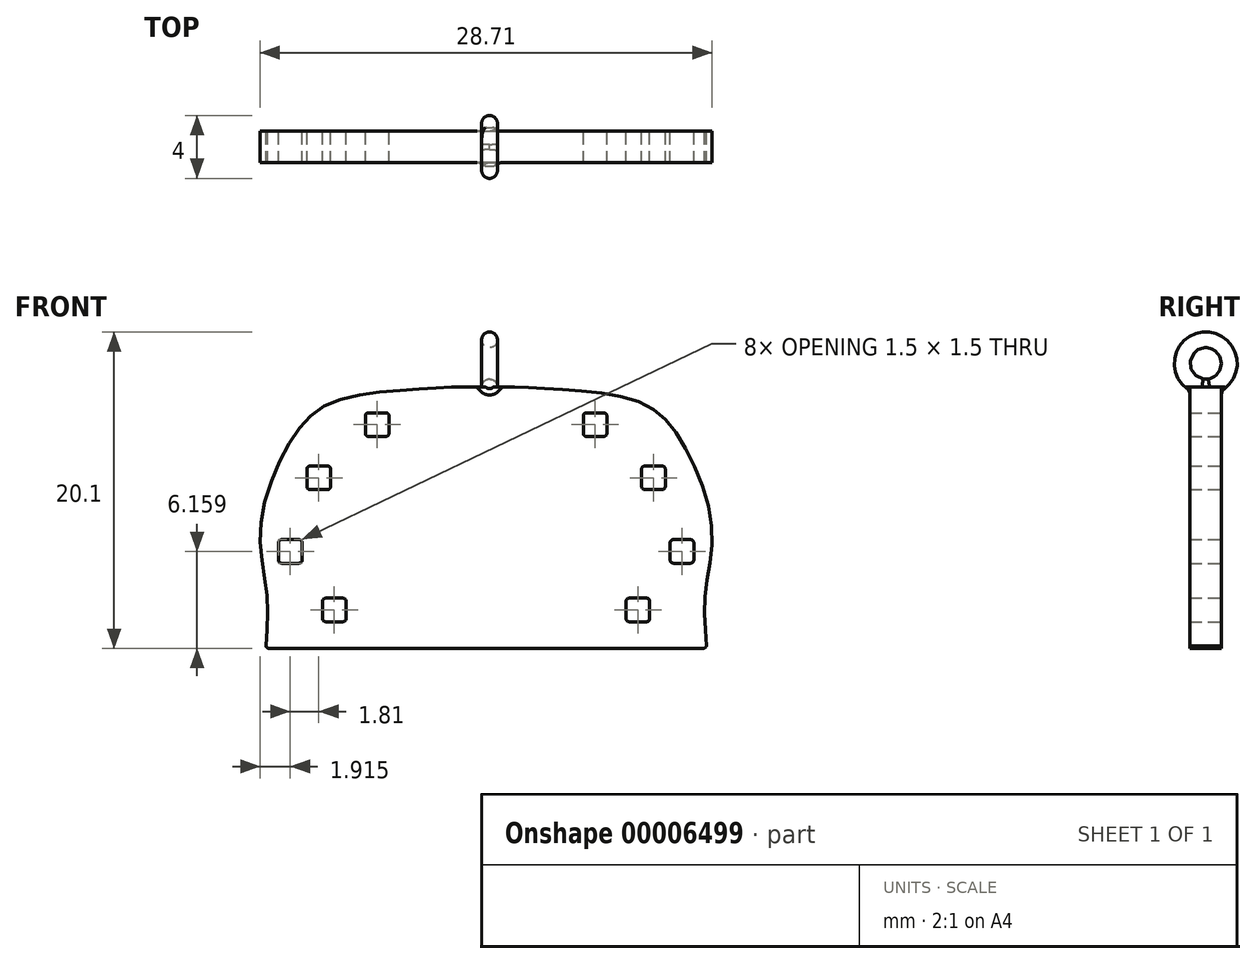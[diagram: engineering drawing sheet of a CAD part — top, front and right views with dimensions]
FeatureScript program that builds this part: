
annotation { "Feature Type Name" : "Feature", "Feature Type Description" : "" }
export const myFeature = defineFeature(function(context is Context, id is Id, definition is map)
    precondition{}
    {
        {
            var Q0;
            Q0=qCreatedBy(makeId("Front.planeOp"),FACE);
            var sketch = newSketch(context, id + "F0", { "sketchPlane" : qUnion([Q0])});
            skFitSpline(sketch, "E0.0", {"points": [v(-0.22, 7.86) * mm, v(-1.98, 7.86) * mm, v(-5.46, 7.65) * mm, v(-10.21, 6.79) * mm, v(-12.74, 4.21) * mm, v(-14.55, -0.98) * mm, v(-14.16, -5.19) * mm, v(-14.22, -8.75) * mm]});
            skFitSpline(sketch, "E0.1", {"points": [v(13.78, -8.75) * mm, v(13.72, -5.19) * mm, v(14.11, -0.98) * mm, v(12.31, 4.21) * mm, v(9.78, 6.79) * mm, v(5.03, 7.65) * mm, v(1.55, 7.86) * mm, v(-0.22, 7.86) * mm]});
            skFitSpline(sketch, "E0.2", {"points": [v(-1.13, 7.85) * mm, v(-0.88, 7.85) * mm, v(-0.64, 7.86) * mm, v(-0.39, 7.86) * mm]});
            skFitSpline(sketch, "E0.3", {"points": [v(-0.04, 7.86) * mm, v(0.2, 7.86) * mm, v(0.45, 7.85) * mm, v(0.7, 7.85) * mm]});
            skArc(sketch, "E0.4", {"start": v(-14.21, -8.54) * mm, "mid": v(-14.16, -8.69) * mm, "end": v(-14.01, -8.75) * mm});
            skArc(sketch, "E1.0", {"start": v(13.58, -8.75) * mm, "mid": v(13.72, -8.69) * mm, "end": v(13.78, -8.54) * mm});
            skLineSegment(sketch, "E2.0", {"start": v(-14.01, -8.75) * mm, "end": v(13.58, -8.75) * mm});
            skFitSpline(sketch, "E3.0", {"points": [v(-0.22, 5.42) * mm, v(-1.29, 5.42) * mm, v(-3.2, 5.36) * mm, v(-6.1, 4.36) * mm, v(-8.13, 1.08) * mm, v(-8.75, -3.32) * mm, v(-8.21, -6.4) * mm, v(-7.84, -7.75) * mm]});
            skFitSpline(sketch, "E3.1", {"points": [v(7.4, -7.75) * mm, v(7.78, -6.4) * mm, v(8.32, -3.32) * mm, v(7.7, 1.08) * mm, v(5.66, 4.36) * mm, v(2.76, 5.36) * mm, v(0.86, 5.42) * mm, v(-0.22, 5.42) * mm]});
            skLineSegment(sketch, "E3.2", {"start": v(-7.69, -7.75) * mm, "end": v(7.25, -7.75) * mm});
            skArc(sketch, "E3.3", {"start": v(7.45, -7.6) * mm, "mid": v(7.38, -7.7) * mm, "end": v(7.25, -7.75) * mm});
            skArc(sketch, "E3.4", {"start": v(-7.69, -7.75) * mm, "mid": v(-7.8, -7.7) * mm, "end": v(-7.88, -7.6) * mm});
            skLineSegment(sketch, "E4.0", {"start": v(-10.4, -7.06) * mm, "end": v(-9.3, -7.06) * mm});
            skArc(sketch, "E4.1", {"start": v(-9.1, -6.86) * mm, "mid": v(-9.16, -7) * mm, "end": v(-9.3, -7.06) * mm});
            skLineSegment(sketch, "E4.2", {"start": v(-9.1, -6.86) * mm, "end": v(-9.1, -5.76) * mm});
            skArc(sketch, "E4.3", {"start": v(-9.3, -5.56) * mm, "mid": v(-9.16, -5.62) * mm, "end": v(-9.1, -5.76) * mm});
            skLineSegment(sketch, "E4.4", {"start": v(-9.3, -5.56) * mm, "end": v(-10.4, -5.56) * mm});
            skLineSegment(sketch, "E4.5", {"start": v(-10.6, -5.76) * mm, "end": v(-10.6, -6.86) * mm});
            skArc(sketch, "E4.6", {"start": v(-10.4, -7.06) * mm, "mid": v(-10.55, -7) * mm, "end": v(-10.6, -6.86) * mm});
            skArc(sketch, "E4.7", {"start": v(-10.6, -5.76) * mm, "mid": v(-10.55, -5.62) * mm, "end": v(-10.4, -5.56) * mm});
            skLineSegment(sketch, "E5.0", {"start": v(-12.1, -1.84) * mm, "end": v(-13.2, -1.84) * mm});
            skArc(sketch, "E5.1", {"start": v(-12.1, -1.84) * mm, "mid": v(-11.96, -1.9) * mm, "end": v(-11.9, -2.04) * mm});
            skLineSegment(sketch, "E5.2", {"start": v(-11.9, -3.14) * mm, "end": v(-11.9, -2.04) * mm});
            skArc(sketch, "E5.3", {"start": v(-11.9, -3.14) * mm, "mid": v(-11.96, -3.28) * mm, "end": v(-12.1, -3.34) * mm});
            skLineSegment(sketch, "E5.4", {"start": v(-13.2, -3.34) * mm, "end": v(-12.1, -3.34) * mm});
            skArc(sketch, "E5.5", {"start": v(-13.4, -2.04) * mm, "mid": v(-13.35, -1.9) * mm, "end": v(-13.2, -1.84) * mm});
            skLineSegment(sketch, "E5.6", {"start": v(-13.4, -2.04) * mm, "end": v(-13.4, -3.14) * mm});
            skArc(sketch, "E5.7", {"start": v(-13.2, -3.34) * mm, "mid": v(-13.35, -3.28) * mm, "end": v(-13.4, -3.14) * mm});
            skLineSegment(sketch, "E6.0", {"start": v(-10.3, 2.83) * mm, "end": v(-11.4, 2.83) * mm});
            skArc(sketch, "E6.1", {"start": v(-11.6, 2.63) * mm, "mid": v(-11.54, 2.77) * mm, "end": v(-11.4, 2.83) * mm});
            skLineSegment(sketch, "E6.2", {"start": v(-11.6, 2.63) * mm, "end": v(-11.6, 1.53) * mm});
            skArc(sketch, "E6.3", {"start": v(-11.4, 1.33) * mm, "mid": v(-11.54, 1.4) * mm, "end": v(-11.6, 1.53) * mm});
            skLineSegment(sketch, "E6.4", {"start": v(-11.4, 1.33) * mm, "end": v(-10.3, 1.33) * mm});
            skArc(sketch, "E6.5", {"start": v(-10.1, 1.53) * mm, "mid": v(-10.15, 1.4) * mm, "end": v(-10.3, 1.33) * mm});
            skLineSegment(sketch, "E6.6", {"start": v(-10.1, 1.53) * mm, "end": v(-10.1, 2.63) * mm});
            skArc(sketch, "E6.7", {"start": v(-10.3, 2.83) * mm, "mid": v(-10.15, 2.77) * mm, "end": v(-10.1, 2.63) * mm});
            skLineSegment(sketch, "E7.0", {"start": v(-6.59, 6.21) * mm, "end": v(-7.69, 6.21) * mm});
            skLineSegment(sketch, "E7.1", {"start": v(-7.69, 4.71) * mm, "end": v(-6.59, 4.71) * mm});
            skArc(sketch, "E7.2", {"start": v(-6.39, 4.91) * mm, "mid": v(-6.44, 4.77) * mm, "end": v(-6.59, 4.71) * mm});
            skLineSegment(sketch, "E7.3", {"start": v(-6.39, 4.91) * mm, "end": v(-6.39, 6.01) * mm});
            skArc(sketch, "E7.4", {"start": v(-6.59, 6.21) * mm, "mid": v(-6.44, 6.15) * mm, "end": v(-6.39, 6.01) * mm});
            skArc(sketch, "E7.5", {"start": v(-7.89, 6.01) * mm, "mid": v(-7.83, 6.15) * mm, "end": v(-7.69, 6.21) * mm});
            skLineSegment(sketch, "E7.6", {"start": v(-7.89, 6.01) * mm, "end": v(-7.89, 4.91) * mm});
            skArc(sketch, "E7.7", {"start": v(-7.69, 4.71) * mm, "mid": v(-7.83, 4.77) * mm, "end": v(-7.89, 4.91) * mm});
            skLineSegment(sketch, "E8.0", {"start": v(7.25, 6.21) * mm, "end": v(6.15, 6.21) * mm});
            skArc(sketch, "E8.1", {"start": v(5.95, 6.01) * mm, "mid": v(6.01, 6.15) * mm, "end": v(6.15, 6.21) * mm});
            skLineSegment(sketch, "E8.2", {"start": v(5.95, 6.01) * mm, "end": v(5.95, 4.91) * mm});
            skArc(sketch, "E8.3", {"start": v(6.15, 4.71) * mm, "mid": v(6.01, 4.77) * mm, "end": v(5.95, 4.91) * mm});
            skLineSegment(sketch, "E8.4", {"start": v(6.15, 4.71) * mm, "end": v(7.25, 4.71) * mm});
            skArc(sketch, "E8.5", {"start": v(7.45, 4.91) * mm, "mid": v(7.4, 4.77) * mm, "end": v(7.25, 4.71) * mm});
            skLineSegment(sketch, "E8.6", {"start": v(7.45, 4.91) * mm, "end": v(7.45, 6.01) * mm});
            skArc(sketch, "E8.7", {"start": v(7.25, 6.21) * mm, "mid": v(7.4, 6.15) * mm, "end": v(7.45, 6.01) * mm});
            skLineSegment(sketch, "E9.0", {"start": v(10.96, 2.83) * mm, "end": v(9.86, 2.83) * mm});
            skArc(sketch, "E9.1", {"start": v(9.66, 2.63) * mm, "mid": v(9.72, 2.77) * mm, "end": v(9.86, 2.83) * mm});
            skLineSegment(sketch, "E9.2", {"start": v(9.66, 2.63) * mm, "end": v(9.66, 1.53) * mm});
            skArc(sketch, "E9.3", {"start": v(9.86, 1.33) * mm, "mid": v(9.72, 1.4) * mm, "end": v(9.66, 1.53) * mm});
            skLineSegment(sketch, "E9.4", {"start": v(9.86, 1.33) * mm, "end": v(10.96, 1.33) * mm});
            skArc(sketch, "E9.5", {"start": v(11.16, 1.53) * mm, "mid": v(11.1, 1.4) * mm, "end": v(10.96, 1.33) * mm});
            skLineSegment(sketch, "E9.6", {"start": v(11.16, 1.53) * mm, "end": v(11.16, 2.63) * mm});
            skArc(sketch, "E9.7", {"start": v(10.96, 2.83) * mm, "mid": v(11.1, 2.77) * mm, "end": v(11.16, 2.63) * mm});
            skLineSegment(sketch, "E10.0", {"start": v(12.77, -1.84) * mm, "end": v(11.67, -1.84) * mm});
            skArc(sketch, "E10.1", {"start": v(11.47, -2.04) * mm, "mid": v(11.53, -1.9) * mm, "end": v(11.67, -1.84) * mm});
            skLineSegment(sketch, "E10.2", {"start": v(11.47, -2.04) * mm, "end": v(11.47, -3.14) * mm});
            skArc(sketch, "E10.3", {"start": v(11.67, -3.34) * mm, "mid": v(11.53, -3.28) * mm, "end": v(11.47, -3.14) * mm});
            skLineSegment(sketch, "E10.4", {"start": v(11.67, -3.34) * mm, "end": v(12.77, -3.34) * mm});
            skArc(sketch, "E10.5", {"start": v(12.97, -3.14) * mm, "mid": v(12.91, -3.28) * mm, "end": v(12.77, -3.34) * mm});
            skLineSegment(sketch, "E10.6", {"start": v(12.97, -3.14) * mm, "end": v(12.97, -2.04) * mm});
            skArc(sketch, "E10.7", {"start": v(12.77, -1.84) * mm, "mid": v(12.91, -1.9) * mm, "end": v(12.97, -2.04) * mm});
            skLineSegment(sketch, "E11.0", {"start": v(9.97, -5.56) * mm, "end": v(8.87, -5.56) * mm});
            skArc(sketch, "E11.1", {"start": v(8.67, -5.76) * mm, "mid": v(8.73, -5.62) * mm, "end": v(8.87, -5.56) * mm});
            skLineSegment(sketch, "E11.2", {"start": v(8.67, -5.76) * mm, "end": v(8.67, -6.86) * mm});
            skArc(sketch, "E11.3", {"start": v(8.87, -7.06) * mm, "mid": v(8.73, -7) * mm, "end": v(8.67, -6.86) * mm});
            skLineSegment(sketch, "E11.4", {"start": v(8.87, -7.06) * mm, "end": v(9.97, -7.06) * mm});
            skArc(sketch, "E11.5", {"start": v(10.17, -6.86) * mm, "mid": v(10.12, -7) * mm, "end": v(9.97, -7.06) * mm});
            skLineSegment(sketch, "E11.6", {"start": v(10.17, -6.86) * mm, "end": v(10.17, -5.76) * mm});
            skArc(sketch, "E11.7", {"start": v(9.97, -5.56) * mm, "mid": v(10.12, -5.62) * mm, "end": v(10.17, -5.76) * mm});
            skArc(sketch, "E12", {"start": v(-0.04, 7.86) * mm, "mid": v(-0.22, 7.86) * mm, "end": v(-0.39, 7.86) * mm});
            skSolve(sketch);
        }
        {
            var Q0;
            Q0=makeQuery(id+"F0.imprint","IMPRINT",FACE,{"disambiguationData":[TD([[makeQuery(id+"F0.imprint","IMPRINT",EDGE,{"derivedFrom":sQuery(id+"F0.wireOp",EDGE,"E0.0")}),1.0]])]});
            var Q1;
            Q1=sQuery(id+"F0.wireOp",EDGE,"E0.0");
            var Q2;
            Q2=sQuery(id+"F0.wireOp",EDGE,"E0.1");
            var Q3;
            Q3=sQuery(id+"F0.wireOp",EDGE,"E0.2");
            var Q4;
            Q4=sQuery(id+"F0.wireOp",EDGE,"E0.3");
            var Q5;
            Q5=sQuery(id+"F0.wireOp",EDGE,"E0.4");
            var Q6;
            Q6=sQuery(id+"F0.wireOp",EDGE,"E1.0");
            var Q7;
            Q7=sQuery(id+"F0.wireOp",EDGE,"E2.0");
            var Q8;
            Q8=sQuery(id+"F0.wireOp",EDGE,"E3.0");
            var Q9;
            Q9=sQuery(id+"F0.wireOp",EDGE,"E3.1");
            var Q10;
            Q10=sQuery(id+"F0.wireOp",EDGE,"E3.2");
            var Q11;
            Q11=sQuery(id+"F0.wireOp",EDGE,"E3.3");
            var Q12;
            Q12=sQuery(id+"F0.wireOp",EDGE,"E3.4");
            var Q13;
            Q13=sQuery(id+"F0.wireOp",EDGE,"E4.0");
            var Q14;
            Q14=sQuery(id+"F0.wireOp",EDGE,"E4.1");
            var Q15;
            Q15=sQuery(id+"F0.wireOp",EDGE,"E4.2");
            var Q16;
            Q16=sQuery(id+"F0.wireOp",EDGE,"E4.3");
            var Q17;
            Q17=sQuery(id+"F0.wireOp",EDGE,"E4.4");
            var Q18;
            Q18=sQuery(id+"F0.wireOp",EDGE,"E4.5");
            var Q19;
            Q19=sQuery(id+"F0.wireOp",EDGE,"E4.6");
            var Q20;
            Q20=sQuery(id+"F0.wireOp",EDGE,"E4.7");
            var Q21;
            Q21=sQuery(id+"F0.wireOp",EDGE,"E5.0");
            var Q22;
            Q22=sQuery(id+"F0.wireOp",EDGE,"E5.1");
            var Q23;
            Q23=sQuery(id+"F0.wireOp",EDGE,"E5.2");
            var Q24;
            Q24=sQuery(id+"F0.wireOp",EDGE,"E5.3");
            var Q25;
            Q25=sQuery(id+"F0.wireOp",EDGE,"E5.4");
            var Q26;
            Q26=sQuery(id+"F0.wireOp",EDGE,"E5.5");
            var Q27;
            Q27=sQuery(id+"F0.wireOp",EDGE,"E5.6");
            var Q28;
            Q28=sQuery(id+"F0.wireOp",EDGE,"E5.7");
            var Q29;
            Q29=sQuery(id+"F0.wireOp",EDGE,"E6.0");
            var Q30;
            Q30=sQuery(id+"F0.wireOp",EDGE,"E6.1");
            var Q31;
            Q31=sQuery(id+"F0.wireOp",EDGE,"E6.2");
            var Q32;
            Q32=sQuery(id+"F0.wireOp",EDGE,"E6.3");
            var Q33;
            Q33=sQuery(id+"F0.wireOp",EDGE,"E6.4");
            var Q34;
            Q34=sQuery(id+"F0.wireOp",EDGE,"E6.5");
            var Q35;
            Q35=sQuery(id+"F0.wireOp",EDGE,"E6.6");
            var Q36;
            Q36=sQuery(id+"F0.wireOp",EDGE,"E6.7");
            var Q37;
            Q37=sQuery(id+"F0.wireOp",EDGE,"E7.0");
            var Q38;
            Q38=sQuery(id+"F0.wireOp",EDGE,"E7.1");
            var Q39;
            Q39=sQuery(id+"F0.wireOp",EDGE,"E7.2");
            var Q40;
            Q40=sQuery(id+"F0.wireOp",EDGE,"E7.3");
            var Q41;
            Q41=sQuery(id+"F0.wireOp",EDGE,"E7.4");
            var Q42;
            Q42=sQuery(id+"F0.wireOp",EDGE,"E7.5");
            var Q43;
            Q43=sQuery(id+"F0.wireOp",EDGE,"E7.6");
            var Q44;
            Q44=sQuery(id+"F0.wireOp",EDGE,"E7.7");
            var Q45;
            Q45=sQuery(id+"F0.wireOp",EDGE,"E8.0");
            var Q46;
            Q46=sQuery(id+"F0.wireOp",EDGE,"E8.1");
            var Q47;
            Q47=sQuery(id+"F0.wireOp",EDGE,"E8.2");
            var Q48;
            Q48=sQuery(id+"F0.wireOp",EDGE,"E8.3");
            var Q49;
            Q49=sQuery(id+"F0.wireOp",EDGE,"E8.4");
            var Q50;
            Q50=sQuery(id+"F0.wireOp",EDGE,"E8.5");
            var Q51;
            Q51=sQuery(id+"F0.wireOp",EDGE,"E8.6");
            var Q52;
            Q52=sQuery(id+"F0.wireOp",EDGE,"E8.7");
            var Q53;
            Q53=sQuery(id+"F0.wireOp",EDGE,"E9.0");
            var Q54;
            Q54=sQuery(id+"F0.wireOp",EDGE,"E9.1");
            var Q55;
            Q55=sQuery(id+"F0.wireOp",EDGE,"E9.2");
            var Q56;
            Q56=sQuery(id+"F0.wireOp",EDGE,"E9.3");
            var Q57;
            Q57=sQuery(id+"F0.wireOp",EDGE,"E9.4");
            var Q58;
            Q58=sQuery(id+"F0.wireOp",EDGE,"E9.5");
            var Q59;
            Q59=sQuery(id+"F0.wireOp",EDGE,"E9.6");
            var Q60;
            Q60=sQuery(id+"F0.wireOp",EDGE,"E9.7");
            var Q61;
            Q61=sQuery(id+"F0.wireOp",EDGE,"E10.0");
            var Q62;
            Q62=sQuery(id+"F0.wireOp",EDGE,"E10.1");
            var Q63;
            Q63=sQuery(id+"F0.wireOp",EDGE,"E10.2");
            var Q64;
            Q64=sQuery(id+"F0.wireOp",EDGE,"E10.3");
            var Q65;
            Q65=sQuery(id+"F0.wireOp",EDGE,"E10.4");
            var Q66;
            Q66=sQuery(id+"F0.wireOp",EDGE,"E10.5");
            var Q67;
            Q67=sQuery(id+"F0.wireOp",EDGE,"E10.6");
            var Q68;
            Q68=sQuery(id+"F0.wireOp",EDGE,"E10.7");
            var Q69;
            Q69=sQuery(id+"F0.wireOp",EDGE,"E11.0");
            var Q70;
            Q70=sQuery(id+"F0.wireOp",EDGE,"E11.1");
            var Q71;
            Q71=sQuery(id+"F0.wireOp",EDGE,"E11.2");
            var Q72;
            Q72=sQuery(id+"F0.wireOp",EDGE,"E11.3");
            var Q73;
            Q73=sQuery(id+"F0.wireOp",EDGE,"E11.4");
            var Q74;
            Q74=sQuery(id+"F0.wireOp",EDGE,"E11.5");
            var Q75;
            Q75=sQuery(id+"F0.wireOp",EDGE,"E11.6");
            var Q76;
            Q76=sQuery(id+"F0.wireOp",EDGE,"E11.7");
            var Q77;
            Q77=sQuery(id+"F0.wireOp",EDGE,"E12");
            extrude(context, id + "F1", {"entities" : qUnion([Q0]), "surfaceEntities" : qUnion([Q1, Q2, Q3, Q4, Q5, Q6, Q7, Q8, Q9, Q10, Q11, Q12, Q13, Q14, Q15, Q16, Q17, Q18, Q19, Q20, Q21, Q22, Q23, Q24, Q25, Q26, Q27, Q28, Q29, Q30, Q31, Q32, Q33, Q34, Q35, Q36, Q37, Q38, Q39, Q40, Q41, Q42, Q43, Q44, Q45, Q46, Q47, Q48, Q49, Q50, Q51, Q52, Q53, Q54, Q55, Q56, Q57, Q58, Q59, Q60, Q61, Q62, Q63, Q64, Q65, Q66, Q67, Q68, Q69, Q70, Q71, Q72, Q73, Q74, Q75, Q76, Q77]), "endBound" : BoundingType.SYMMETRIC, "depth" : 2 * mm});
        }
        {
            var Q0;
            Q0=qCreatedBy(makeId("Right.planeOp"),FACE);
            var sketch = newSketch(context, id + "F2", { "sketchPlane" : qUnion([Q0])});
            skCircle(sketch, "E13", {"center": v(0, 9.35) * mm, "radius": 2 * mm});
            skCircle(sketch, "E14", {"center": v(0, 9.35) * mm, "radius": 1 * mm});
            skSolve(sketch);
        }
        {
            var Q0;
            Q0 = qSketchRegion(id + "F2", true);
            extrude(context, id + "F3", {"entities" : qUnion([Q0]), "operationType" : NewBodyOperationType.ADD, "endBound" : BoundingType.SYMMETRIC, "depth" : 1 * mm});
        }
        {
            var Q0;
            Q0=makeQuery(id+"F3.opExtrude","CAP_EDGE",EDGE,{"disambiguationData":[OSD([sQuery(id+"F2.wireOp",EDGE,"E13")])],"isStart":false});
            var Q1;
            Q1=makeQuery(id+"F3.opExtrude","CAP_EDGE",EDGE,{"disambiguationData":[OSD([sQuery(id+"F2.wireOp",EDGE,"E13")])],"isStart":true});
            fillet(context, id + "F4", {"entities" : qUnion([Q0, Q1]), "radius" : 0.5 * mm, "tangentPropagation" : true, "allowEdgeOverflow" : false});
        }
        {
            var Q0;
            Q0=makeQuery(id+"F4.opFillet","BLEND_EDGE",EDGE,{"blendedFrom":[makeQuery(id+"F3.opExtrude","CAP_EDGE",EDGE,{"disambiguationData":[OSD([sQuery(id+"F2.wireOp",EDGE,"E13")])],"isStart":false}),makeQuery(id+"F1.opExtrude","CAP_FACE",FACE,{"disambiguationData":[OSD([sQuery(id+"F0.wireOp",EDGE,"E0.0"),sQuery(id+"F0.wireOp",EDGE,"E0.1"),sQuery(id+"F0.wireOp",EDGE,"E0.2"),sQuery(id+"F0.wireOp",EDGE,"E0.3"),sQuery(id+"F0.wireOp",EDGE,"E0.4"),sQuery(id+"F0.wireOp",EDGE,"E1.0"),sQuery(id+"F0.wireOp",EDGE,"E2.0"),sQuery(id+"F0.wireOp",EDGE,"E3.0"),sQuery(id+"F0.wireOp",EDGE,"E3.1"),sQuery(id+"F0.wireOp",EDGE,"E3.2"),sQuery(id+"F0.wireOp",EDGE,"E3.3"),sQuery(id+"F0.wireOp",EDGE,"E3.4"),sQuery(id+"F0.wireOp",EDGE,"E4.0"),sQuery(id+"F0.wireOp",EDGE,"E4.1"),sQuery(id+"F0.wireOp",EDGE,"E4.2"),sQuery(id+"F0.wireOp",EDGE,"E4.3"),sQuery(id+"F0.wireOp",EDGE,"E4.4"),sQuery(id+"F0.wireOp",EDGE,"E4.5"),sQuery(id+"F0.wireOp",EDGE,"E4.6"),sQuery(id+"F0.wireOp",EDGE,"E4.7"),sQuery(id+"F0.wireOp",EDGE,"E5.0"),sQuery(id+"F0.wireOp",EDGE,"E5.1"),sQuery(id+"F0.wireOp",EDGE,"E5.2"),sQuery(id+"F0.wireOp",EDGE,"E5.3"),sQuery(id+"F0.wireOp",EDGE,"E5.4"),sQuery(id+"F0.wireOp",EDGE,"E5.5"),sQuery(id+"F0.wireOp",EDGE,"E5.6"),sQuery(id+"F0.wireOp",EDGE,"E5.7"),sQuery(id+"F0.wireOp",EDGE,"E6.0"),sQuery(id+"F0.wireOp",EDGE,"E6.1"),sQuery(id+"F0.wireOp",EDGE,"E6.2"),sQuery(id+"F0.wireOp",EDGE,"E6.3"),sQuery(id+"F0.wireOp",EDGE,"E6.4"),sQuery(id+"F0.wireOp",EDGE,"E6.5"),sQuery(id+"F0.wireOp",EDGE,"E6.6"),sQuery(id+"F0.wireOp",EDGE,"E6.7"),sQuery(id+"F0.wireOp",EDGE,"E7.0"),sQuery(id+"F0.wireOp",EDGE,"E7.1"),sQuery(id+"F0.wireOp",EDGE,"E7.2"),sQuery(id+"F0.wireOp",EDGE,"E7.3"),sQuery(id+"F0.wireOp",EDGE,"E7.4"),sQuery(id+"F0.wireOp",EDGE,"E7.5"),sQuery(id+"F0.wireOp",EDGE,"E7.6"),sQuery(id+"F0.wireOp",EDGE,"E7.7"),sQuery(id+"F0.wireOp",EDGE,"E8.0"),sQuery(id+"F0.wireOp",EDGE,"E8.1"),sQuery(id+"F0.wireOp",EDGE,"E8.2"),sQuery(id+"F0.wireOp",EDGE,"E8.3"),sQuery(id+"F0.wireOp",EDGE,"E8.4"),sQuery(id+"F0.wireOp",EDGE,"E8.5"),sQuery(id+"F0.wireOp",EDGE,"E8.6"),sQuery(id+"F0.wireOp",EDGE,"E8.7"),sQuery(id+"F0.wireOp",EDGE,"E9.0"),sQuery(id+"F0.wireOp",EDGE,"E9.1"),sQuery(id+"F0.wireOp",EDGE,"E9.2"),sQuery(id+"F0.wireOp",EDGE,"E9.3"),sQuery(id+"F0.wireOp",EDGE,"E9.4"),sQuery(id+"F0.wireOp",EDGE,"E9.5"),sQuery(id+"F0.wireOp",EDGE,"E9.6"),sQuery(id+"F0.wireOp",EDGE,"E9.7"),sQuery(id+"F0.wireOp",EDGE,"E10.0"),sQuery(id+"F0.wireOp",EDGE,"E10.1"),sQuery(id+"F0.wireOp",EDGE,"E10.2"),sQuery(id+"F0.wireOp",EDGE,"E10.3"),sQuery(id+"F0.wireOp",EDGE,"E10.4"),sQuery(id+"F0.wireOp",EDGE,"E10.5"),sQuery(id+"F0.wireOp",EDGE,"E10.6"),sQuery(id+"F0.wireOp",EDGE,"E10.7"),sQuery(id+"F0.wireOp",EDGE,"E11.0"),sQuery(id+"F0.wireOp",EDGE,"E11.1"),sQuery(id+"F0.wireOp",EDGE,"E11.2"),sQuery(id+"F0.wireOp",EDGE,"E11.3"),sQuery(id+"F0.wireOp",EDGE,"E11.4"),sQuery(id+"F0.wireOp",EDGE,"E11.5"),sQuery(id+"F0.wireOp",EDGE,"E11.6"),sQuery(id+"F0.wireOp",EDGE,"E11.7"),sQuery(id+"F0.wireOp",EDGE,"E12")])],"isStart":false})],"blendedInto":[makeQuery(id+"F1.opExtrude","CAP_FACE",FACE,{"disambiguationData":[OSD([sQuery(id+"F0.wireOp",EDGE,"E0.0"),sQuery(id+"F0.wireOp",EDGE,"E0.1"),sQuery(id+"F0.wireOp",EDGE,"E0.2"),sQuery(id+"F0.wireOp",EDGE,"E0.3"),sQuery(id+"F0.wireOp",EDGE,"E0.4"),sQuery(id+"F0.wireOp",EDGE,"E1.0"),sQuery(id+"F0.wireOp",EDGE,"E2.0"),sQuery(id+"F0.wireOp",EDGE,"E3.0"),sQuery(id+"F0.wireOp",EDGE,"E3.1"),sQuery(id+"F0.wireOp",EDGE,"E3.2"),sQuery(id+"F0.wireOp",EDGE,"E3.3"),sQuery(id+"F0.wireOp",EDGE,"E3.4"),sQuery(id+"F0.wireOp",EDGE,"E4.0"),sQuery(id+"F0.wireOp",EDGE,"E4.1"),sQuery(id+"F0.wireOp",EDGE,"E4.2"),sQuery(id+"F0.wireOp",EDGE,"E4.3"),sQuery(id+"F0.wireOp",EDGE,"E4.4"),sQuery(id+"F0.wireOp",EDGE,"E4.5"),sQuery(id+"F0.wireOp",EDGE,"E4.6"),sQuery(id+"F0.wireOp",EDGE,"E4.7"),sQuery(id+"F0.wireOp",EDGE,"E5.0"),sQuery(id+"F0.wireOp",EDGE,"E5.1"),sQuery(id+"F0.wireOp",EDGE,"E5.2"),sQuery(id+"F0.wireOp",EDGE,"E5.3"),sQuery(id+"F0.wireOp",EDGE,"E5.4"),sQuery(id+"F0.wireOp",EDGE,"E5.5"),sQuery(id+"F0.wireOp",EDGE,"E5.6"),sQuery(id+"F0.wireOp",EDGE,"E5.7"),sQuery(id+"F0.wireOp",EDGE,"E6.0"),sQuery(id+"F0.wireOp",EDGE,"E6.1"),sQuery(id+"F0.wireOp",EDGE,"E6.2"),sQuery(id+"F0.wireOp",EDGE,"E6.3"),sQuery(id+"F0.wireOp",EDGE,"E6.4"),sQuery(id+"F0.wireOp",EDGE,"E6.5"),sQuery(id+"F0.wireOp",EDGE,"E6.6"),sQuery(id+"F0.wireOp",EDGE,"E6.7"),sQuery(id+"F0.wireOp",EDGE,"E7.0"),sQuery(id+"F0.wireOp",EDGE,"E7.1"),sQuery(id+"F0.wireOp",EDGE,"E7.2"),sQuery(id+"F0.wireOp",EDGE,"E7.3"),sQuery(id+"F0.wireOp",EDGE,"E7.4"),sQuery(id+"F0.wireOp",EDGE,"E7.5"),sQuery(id+"F0.wireOp",EDGE,"E7.6"),sQuery(id+"F0.wireOp",EDGE,"E7.7"),sQuery(id+"F0.wireOp",EDGE,"E8.0"),sQuery(id+"F0.wireOp",EDGE,"E8.1"),sQuery(id+"F0.wireOp",EDGE,"E8.2"),sQuery(id+"F0.wireOp",EDGE,"E8.3"),sQuery(id+"F0.wireOp",EDGE,"E8.4"),sQuery(id+"F0.wireOp",EDGE,"E8.5"),sQuery(id+"F0.wireOp",EDGE,"E8.6"),sQuery(id+"F0.wireOp",EDGE,"E8.7"),sQuery(id+"F0.wireOp",EDGE,"E9.0"),sQuery(id+"F0.wireOp",EDGE,"E9.1"),sQuery(id+"F0.wireOp",EDGE,"E9.2"),sQuery(id+"F0.wireOp",EDGE,"E9.3"),sQuery(id+"F0.wireOp",EDGE,"E9.4"),sQuery(id+"F0.wireOp",EDGE,"E9.5"),sQuery(id+"F0.wireOp",EDGE,"E9.6"),sQuery(id+"F0.wireOp",EDGE,"E9.7"),sQuery(id+"F0.wireOp",EDGE,"E10.0"),sQuery(id+"F0.wireOp",EDGE,"E10.1"),sQuery(id+"F0.wireOp",EDGE,"E10.2"),sQuery(id+"F0.wireOp",EDGE,"E10.3"),sQuery(id+"F0.wireOp",EDGE,"E10.4"),sQuery(id+"F0.wireOp",EDGE,"E10.5"),sQuery(id+"F0.wireOp",EDGE,"E10.6"),sQuery(id+"F0.wireOp",EDGE,"E10.7"),sQuery(id+"F0.wireOp",EDGE,"E11.0"),sQuery(id+"F0.wireOp",EDGE,"E11.1"),sQuery(id+"F0.wireOp",EDGE,"E11.2"),sQuery(id+"F0.wireOp",EDGE,"E11.3"),sQuery(id+"F0.wireOp",EDGE,"E11.4"),sQuery(id+"F0.wireOp",EDGE,"E11.5"),sQuery(id+"F0.wireOp",EDGE,"E11.6"),sQuery(id+"F0.wireOp",EDGE,"E11.7"),sQuery(id+"F0.wireOp",EDGE,"E12")])],"isStart":false})]});
            var Q1;
            Q1=makeQuery(id+"F4.opFillet","BLEND_EDGE",EDGE,{"blendedFrom":[makeQuery(id+"F3.opExtrude","CAP_EDGE",EDGE,{"disambiguationData":[OSD([sQuery(id+"F2.wireOp",EDGE,"E13")])],"isStart":true}),makeQuery(id+"F1.opExtrude","CAP_FACE",FACE,{"disambiguationData":[OSD([sQuery(id+"F0.wireOp",EDGE,"E0.0"),sQuery(id+"F0.wireOp",EDGE,"E0.1"),sQuery(id+"F0.wireOp",EDGE,"E0.2"),sQuery(id+"F0.wireOp",EDGE,"E0.3"),sQuery(id+"F0.wireOp",EDGE,"E0.4"),sQuery(id+"F0.wireOp",EDGE,"E1.0"),sQuery(id+"F0.wireOp",EDGE,"E2.0"),sQuery(id+"F0.wireOp",EDGE,"E3.0"),sQuery(id+"F0.wireOp",EDGE,"E3.1"),sQuery(id+"F0.wireOp",EDGE,"E3.2"),sQuery(id+"F0.wireOp",EDGE,"E3.3"),sQuery(id+"F0.wireOp",EDGE,"E3.4"),sQuery(id+"F0.wireOp",EDGE,"E4.0"),sQuery(id+"F0.wireOp",EDGE,"E4.1"),sQuery(id+"F0.wireOp",EDGE,"E4.2"),sQuery(id+"F0.wireOp",EDGE,"E4.3"),sQuery(id+"F0.wireOp",EDGE,"E4.4"),sQuery(id+"F0.wireOp",EDGE,"E4.5"),sQuery(id+"F0.wireOp",EDGE,"E4.6"),sQuery(id+"F0.wireOp",EDGE,"E4.7"),sQuery(id+"F0.wireOp",EDGE,"E5.0"),sQuery(id+"F0.wireOp",EDGE,"E5.1"),sQuery(id+"F0.wireOp",EDGE,"E5.2"),sQuery(id+"F0.wireOp",EDGE,"E5.3"),sQuery(id+"F0.wireOp",EDGE,"E5.4"),sQuery(id+"F0.wireOp",EDGE,"E5.5"),sQuery(id+"F0.wireOp",EDGE,"E5.6"),sQuery(id+"F0.wireOp",EDGE,"E5.7"),sQuery(id+"F0.wireOp",EDGE,"E6.0"),sQuery(id+"F0.wireOp",EDGE,"E6.1"),sQuery(id+"F0.wireOp",EDGE,"E6.2"),sQuery(id+"F0.wireOp",EDGE,"E6.3"),sQuery(id+"F0.wireOp",EDGE,"E6.4"),sQuery(id+"F0.wireOp",EDGE,"E6.5"),sQuery(id+"F0.wireOp",EDGE,"E6.6"),sQuery(id+"F0.wireOp",EDGE,"E6.7"),sQuery(id+"F0.wireOp",EDGE,"E7.0"),sQuery(id+"F0.wireOp",EDGE,"E7.1"),sQuery(id+"F0.wireOp",EDGE,"E7.2"),sQuery(id+"F0.wireOp",EDGE,"E7.3"),sQuery(id+"F0.wireOp",EDGE,"E7.4"),sQuery(id+"F0.wireOp",EDGE,"E7.5"),sQuery(id+"F0.wireOp",EDGE,"E7.6"),sQuery(id+"F0.wireOp",EDGE,"E7.7"),sQuery(id+"F0.wireOp",EDGE,"E8.0"),sQuery(id+"F0.wireOp",EDGE,"E8.1"),sQuery(id+"F0.wireOp",EDGE,"E8.2"),sQuery(id+"F0.wireOp",EDGE,"E8.3"),sQuery(id+"F0.wireOp",EDGE,"E8.4"),sQuery(id+"F0.wireOp",EDGE,"E8.5"),sQuery(id+"F0.wireOp",EDGE,"E8.6"),sQuery(id+"F0.wireOp",EDGE,"E8.7"),sQuery(id+"F0.wireOp",EDGE,"E9.0"),sQuery(id+"F0.wireOp",EDGE,"E9.1"),sQuery(id+"F0.wireOp",EDGE,"E9.2"),sQuery(id+"F0.wireOp",EDGE,"E9.3"),sQuery(id+"F0.wireOp",EDGE,"E9.4"),sQuery(id+"F0.wireOp",EDGE,"E9.5"),sQuery(id+"F0.wireOp",EDGE,"E9.6"),sQuery(id+"F0.wireOp",EDGE,"E9.7"),sQuery(id+"F0.wireOp",EDGE,"E10.0"),sQuery(id+"F0.wireOp",EDGE,"E10.1"),sQuery(id+"F0.wireOp",EDGE,"E10.2"),sQuery(id+"F0.wireOp",EDGE,"E10.3"),sQuery(id+"F0.wireOp",EDGE,"E10.4"),sQuery(id+"F0.wireOp",EDGE,"E10.5"),sQuery(id+"F0.wireOp",EDGE,"E10.6"),sQuery(id+"F0.wireOp",EDGE,"E10.7"),sQuery(id+"F0.wireOp",EDGE,"E11.0"),sQuery(id+"F0.wireOp",EDGE,"E11.1"),sQuery(id+"F0.wireOp",EDGE,"E11.2"),sQuery(id+"F0.wireOp",EDGE,"E11.3"),sQuery(id+"F0.wireOp",EDGE,"E11.4"),sQuery(id+"F0.wireOp",EDGE,"E11.5"),sQuery(id+"F0.wireOp",EDGE,"E11.6"),sQuery(id+"F0.wireOp",EDGE,"E11.7"),sQuery(id+"F0.wireOp",EDGE,"E12")])],"isStart":true})],"blendedInto":[makeQuery(id+"F1.opExtrude","CAP_FACE",FACE,{"disambiguationData":[OSD([sQuery(id+"F0.wireOp",EDGE,"E0.0"),sQuery(id+"F0.wireOp",EDGE,"E0.1"),sQuery(id+"F0.wireOp",EDGE,"E0.2"),sQuery(id+"F0.wireOp",EDGE,"E0.3"),sQuery(id+"F0.wireOp",EDGE,"E0.4"),sQuery(id+"F0.wireOp",EDGE,"E1.0"),sQuery(id+"F0.wireOp",EDGE,"E2.0"),sQuery(id+"F0.wireOp",EDGE,"E3.0"),sQuery(id+"F0.wireOp",EDGE,"E3.1"),sQuery(id+"F0.wireOp",EDGE,"E3.2"),sQuery(id+"F0.wireOp",EDGE,"E3.3"),sQuery(id+"F0.wireOp",EDGE,"E3.4"),sQuery(id+"F0.wireOp",EDGE,"E4.0"),sQuery(id+"F0.wireOp",EDGE,"E4.1"),sQuery(id+"F0.wireOp",EDGE,"E4.2"),sQuery(id+"F0.wireOp",EDGE,"E4.3"),sQuery(id+"F0.wireOp",EDGE,"E4.4"),sQuery(id+"F0.wireOp",EDGE,"E4.5"),sQuery(id+"F0.wireOp",EDGE,"E4.6"),sQuery(id+"F0.wireOp",EDGE,"E4.7"),sQuery(id+"F0.wireOp",EDGE,"E5.0"),sQuery(id+"F0.wireOp",EDGE,"E5.1"),sQuery(id+"F0.wireOp",EDGE,"E5.2"),sQuery(id+"F0.wireOp",EDGE,"E5.3"),sQuery(id+"F0.wireOp",EDGE,"E5.4"),sQuery(id+"F0.wireOp",EDGE,"E5.5"),sQuery(id+"F0.wireOp",EDGE,"E5.6"),sQuery(id+"F0.wireOp",EDGE,"E5.7"),sQuery(id+"F0.wireOp",EDGE,"E6.0"),sQuery(id+"F0.wireOp",EDGE,"E6.1"),sQuery(id+"F0.wireOp",EDGE,"E6.2"),sQuery(id+"F0.wireOp",EDGE,"E6.3"),sQuery(id+"F0.wireOp",EDGE,"E6.4"),sQuery(id+"F0.wireOp",EDGE,"E6.5"),sQuery(id+"F0.wireOp",EDGE,"E6.6"),sQuery(id+"F0.wireOp",EDGE,"E6.7"),sQuery(id+"F0.wireOp",EDGE,"E7.0"),sQuery(id+"F0.wireOp",EDGE,"E7.1"),sQuery(id+"F0.wireOp",EDGE,"E7.2"),sQuery(id+"F0.wireOp",EDGE,"E7.3"),sQuery(id+"F0.wireOp",EDGE,"E7.4"),sQuery(id+"F0.wireOp",EDGE,"E7.5"),sQuery(id+"F0.wireOp",EDGE,"E7.6"),sQuery(id+"F0.wireOp",EDGE,"E7.7"),sQuery(id+"F0.wireOp",EDGE,"E8.0"),sQuery(id+"F0.wireOp",EDGE,"E8.1"),sQuery(id+"F0.wireOp",EDGE,"E8.2"),sQuery(id+"F0.wireOp",EDGE,"E8.3"),sQuery(id+"F0.wireOp",EDGE,"E8.4"),sQuery(id+"F0.wireOp",EDGE,"E8.5"),sQuery(id+"F0.wireOp",EDGE,"E8.6"),sQuery(id+"F0.wireOp",EDGE,"E8.7"),sQuery(id+"F0.wireOp",EDGE,"E9.0"),sQuery(id+"F0.wireOp",EDGE,"E9.1"),sQuery(id+"F0.wireOp",EDGE,"E9.2"),sQuery(id+"F0.wireOp",EDGE,"E9.3"),sQuery(id+"F0.wireOp",EDGE,"E9.4"),sQuery(id+"F0.wireOp",EDGE,"E9.5"),sQuery(id+"F0.wireOp",EDGE,"E9.6"),sQuery(id+"F0.wireOp",EDGE,"E9.7"),sQuery(id+"F0.wireOp",EDGE,"E10.0"),sQuery(id+"F0.wireOp",EDGE,"E10.1"),sQuery(id+"F0.wireOp",EDGE,"E10.2"),sQuery(id+"F0.wireOp",EDGE,"E10.3"),sQuery(id+"F0.wireOp",EDGE,"E10.4"),sQuery(id+"F0.wireOp",EDGE,"E10.5"),sQuery(id+"F0.wireOp",EDGE,"E10.6"),sQuery(id+"F0.wireOp",EDGE,"E10.7"),sQuery(id+"F0.wireOp",EDGE,"E11.0"),sQuery(id+"F0.wireOp",EDGE,"E11.1"),sQuery(id+"F0.wireOp",EDGE,"E11.2"),sQuery(id+"F0.wireOp",EDGE,"E11.3"),sQuery(id+"F0.wireOp",EDGE,"E11.4"),sQuery(id+"F0.wireOp",EDGE,"E11.5"),sQuery(id+"F0.wireOp",EDGE,"E11.6"),sQuery(id+"F0.wireOp",EDGE,"E11.7"),sQuery(id+"F0.wireOp",EDGE,"E12")])],"isStart":true})]});
            fillet(context, id + "F5", {"entities" : qUnion([Q0, Q1]), "radius" : 0.5 * mm, "tangentPropagation" : true, "allowEdgeOverflow" : false});
        }
        {
            var Q0;
            Q0=makeQuery(id+"F3.opExtrude","CAP_EDGE",EDGE,{"disambiguationData":[OSD([sQuery(id+"F2.wireOp",EDGE,"E14")])],"isStart":false});
            var Q1;
            Q1=makeQuery(id+"F3.opExtrude","CAP_EDGE",EDGE,{"disambiguationData":[OSD([sQuery(id+"F2.wireOp",EDGE,"E14")])],"isStart":true});
            fillet(context, id + "F6", {"entities" : qUnion([Q0, Q1]), "radius" : 0.5 * mm, "tangentPropagation" : true, "allowEdgeOverflow" : false});
        }
    });
